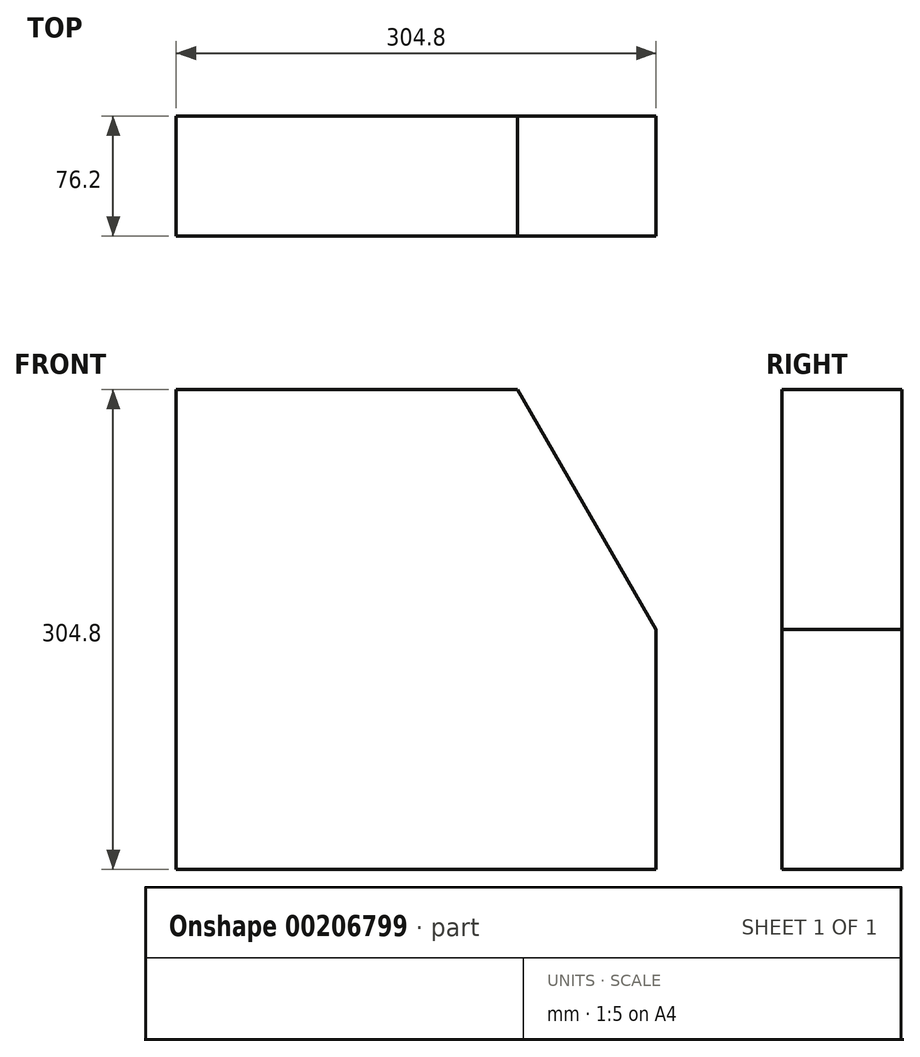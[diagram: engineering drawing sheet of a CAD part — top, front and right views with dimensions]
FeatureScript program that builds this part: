
annotation { "Feature Type Name" : "Feature", "Feature Type Description" : "" }
export const myFeature = defineFeature(function(context is Context, id is Id, definition is map)
    precondition{}
    {
        {
            var Q0;
            Q0=qCreatedBy(makeId("Front.planeOp"),FACE);
            var sketch = newSketch(context, id + "F0", { "sketchPlane" : qUnion([Q0])});
            skLineSegment(sketch, "E0", {"start": v(0, 0) * mm, "end": v(0, 304.8) * mm});
            skLineSegment(sketch, "E1", {"start": v(0, 304.8) * mm, "end": v(216.81, 304.8) * mm});
            skLineSegment(sketch, "E2", {"start": v(216.81, 304.8) * mm, "end": v(304.8, 152.4) * mm});
            skLineSegment(sketch, "E3", {"start": v(304.8, 152.4) * mm, "end": v(304.8, 0) * mm});
            skLineSegment(sketch, "E4", {"start": v(304.8, 0) * mm, "end": v(0, 0) * mm});
            skLineSegment(sketch, "E5", {"start": v(304.8, 152.4) * mm, "end": v(0, 152.4) * mm, "construction": true});
            skSolve(sketch);
        }
        {
            var Q0;
            Q0 = qSketchRegion(id + "F0", true);
            extrude(context, id + "F1", {"entities" : qUnion([Q0]), "depth" : 76.2 * mm, "offsetDistance" : 25.4 * mm});
        }
    });
